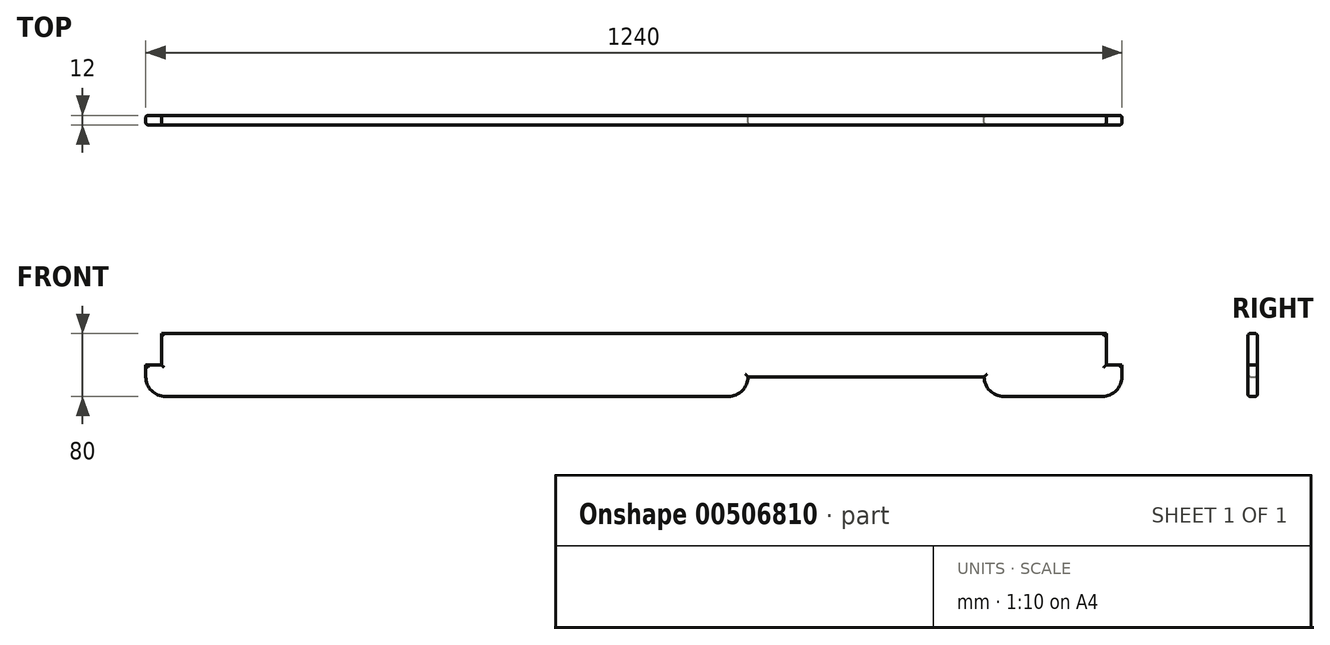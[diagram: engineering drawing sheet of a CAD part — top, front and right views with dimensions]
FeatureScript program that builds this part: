
annotation { "Feature Type Name" : "Feature", "Feature Type Description" : "" }
export const myFeature = defineFeature(function(context is Context, id is Id, definition is map)
    precondition{}
    {
        {
            var Q0;
            Q0=qCreatedBy(makeId("Front.planeOp"),FACE);
            var sketch = newSketch(context, id + "F0", { "sketchPlane" : qUnion([Q0])});
            skLineSegment(sketch, "E0.bottom", {"start": v(-386.61, 66.98) * mm, "end": v(813.39, 66.98) * mm});
            skLineSegment(sketch, "E0.top", {"start": v(-381.61, -13.02) * mm, "end": v(333.39, -13.02) * mm});
            skLineSegment(sketch, "E0.left", {"start": v(-406.61, 26.98) * mm, "end": v(-406.61, 11.98) * mm});
            skLineSegment(sketch, "E0.right", {"start": v(833.39, 26.98) * mm, "end": v(833.39, 11.98) * mm});
            skLineSegment(sketch, "E1.bottom", {"start": v(-406.61, 26.98) * mm, "end": v(-386.61, 26.98) * mm});
            skLineSegment(sketch, "E1.right", {"start": v(-386.61, 26.98) * mm, "end": v(-386.61, 66.98) * mm});
            skLineSegment(sketch, "E2.top", {"start": v(813.39, 26.98) * mm, "end": v(833.39, 26.98) * mm});
            skLineSegment(sketch, "E2.left", {"start": v(813.39, 66.98) * mm, "end": v(813.39, 26.98) * mm});
            skPoint(sketch, "E3.visualSharp", {"position": v(-406.61, -13.02) * mm});
            skArc(sketch, "E3.filletArc", {"start": v(-406.61, 11.98) * mm, "mid": v(-399.29, -5.7) * mm, "end": v(-381.61, -13.02) * mm});
            skPoint(sketch, "E4.visualSharp", {"position": v(833.39, -13.02) * mm});
            skArc(sketch, "E4.filletArc", {"start": v(808.39, -13.02) * mm, "mid": v(826.07, -5.7) * mm, "end": v(833.39, 11.98) * mm});
            skLineSegment(sketch, "E5", {"start": v(808.39, -13.02) * mm, "end": v(658.39, -13.02) * mm, "construction": true});
            skLineSegment(sketch, "E6.trimOffspring", {"start": v(683.39, -13.02) * mm, "end": v(808.39, -13.02) * mm});
            skPoint(sketch, "E7.visualSharp", {"position": v(358.39, -13.02) * mm});
            skArc(sketch, "E7.filletArc", {"start": v(333.39, -13.02) * mm, "mid": v(351.07, -5.7) * mm, "end": v(358.39, 11.98) * mm});
            skPoint(sketch, "E8.visualSharp", {"position": v(658.39, -13.02) * mm});
            skArc(sketch, "E8.filletArc", {"start": v(658.39, 11.98) * mm, "mid": v(665.71, -5.7) * mm, "end": v(683.39, -13.02) * mm});
            skLineSegment(sketch, "E9", {"start": v(358.39, 11.98) * mm, "end": v(658.39, 11.98) * mm});
            skSolve(sketch);
        }
        {
            var Q0;
            Q0=makeQuery(id+"F0.imprint","IMPRINT",FACE,{"disambiguationData":[TD([[makeQuery(id+"F0.imprint","IMPRINT",EDGE,{"derivedFrom":sQuery(id+"F0.wireOp",EDGE,"E0.bottom")}),-1.0]])]});
            extrude(context, id + "F1", {"entities" : qUnion([Q0]), "depth" : 12 * mm});
        }
        {
            var Q0;
            Q0=makeQuery(id+"F1.opExtrude","CAP_FACE",FACE,{"disambiguationData":[OSD([sQuery(id+"F0.wireOp",EDGE,"E0.bottom"),sQuery(id+"F0.wireOp",EDGE,"E0.top"),sQuery(id+"F0.wireOp",EDGE,"E0.left"),sQuery(id+"F0.wireOp",EDGE,"E0.right"),sQuery(id+"F0.wireOp",EDGE,"E1.bottom"),sQuery(id+"F0.wireOp",EDGE,"E1.right"),sQuery(id+"F0.wireOp",EDGE,"E2.top"),sQuery(id+"F0.wireOp",EDGE,"E2.left")])],"isStart":false});
            var sketch = newSketch(context, id + "F2", { "sketchPlane" : qUnion([Q0])});
            skLineSegment(sketch, "E10", {"start": v(-386.61, 66.98) * mm, "end": v(-386.61, 46.98) * mm});
            skLineSegment(sketch, "E11", {"start": v(-386.61, 46.98) * mm, "end": v(213.39, 46.98) * mm});
            skSolve(sketch);
        }
        {
            var Q0;
            Q0=makeQuery(id+"F1.opExtrude","CAP_FACE",FACE,{"disambiguationData":[OSD([sQuery(id+"F0.wireOp",EDGE,"E0.bottom"),sQuery(id+"F0.wireOp",EDGE,"E0.top"),sQuery(id+"F0.wireOp",EDGE,"E0.left"),sQuery(id+"F0.wireOp",EDGE,"E0.right"),sQuery(id+"F0.wireOp",EDGE,"E1.bottom"),sQuery(id+"F0.wireOp",EDGE,"E1.right"),sQuery(id+"F0.wireOp",EDGE,"E2.top"),sQuery(id+"F0.wireOp",EDGE,"E2.left")])],"isStart":false});
            var Q1;
            Q1=makeQuery(id+"F1.opExtrude","CAP_FACE",FACE,{"disambiguationData":[OSD([sQuery(id+"F0.wireOp",EDGE,"E0.bottom"),sQuery(id+"F0.wireOp",EDGE,"E0.top"),sQuery(id+"F0.wireOp",EDGE,"E0.left"),sQuery(id+"F0.wireOp",EDGE,"E0.right"),sQuery(id+"F0.wireOp",EDGE,"E1.bottom"),sQuery(id+"F0.wireOp",EDGE,"E1.right"),sQuery(id+"F0.wireOp",EDGE,"E2.top"),sQuery(id+"F0.wireOp",EDGE,"E2.left")])],"isStart":true});
            fillet(context, id + "F3", {"entities" : qUnion([Q0, Q1]), "radius" : 3 * mm, "tangentPropagation" : true, "allowEdgeOverflow" : false});
        }
    });
